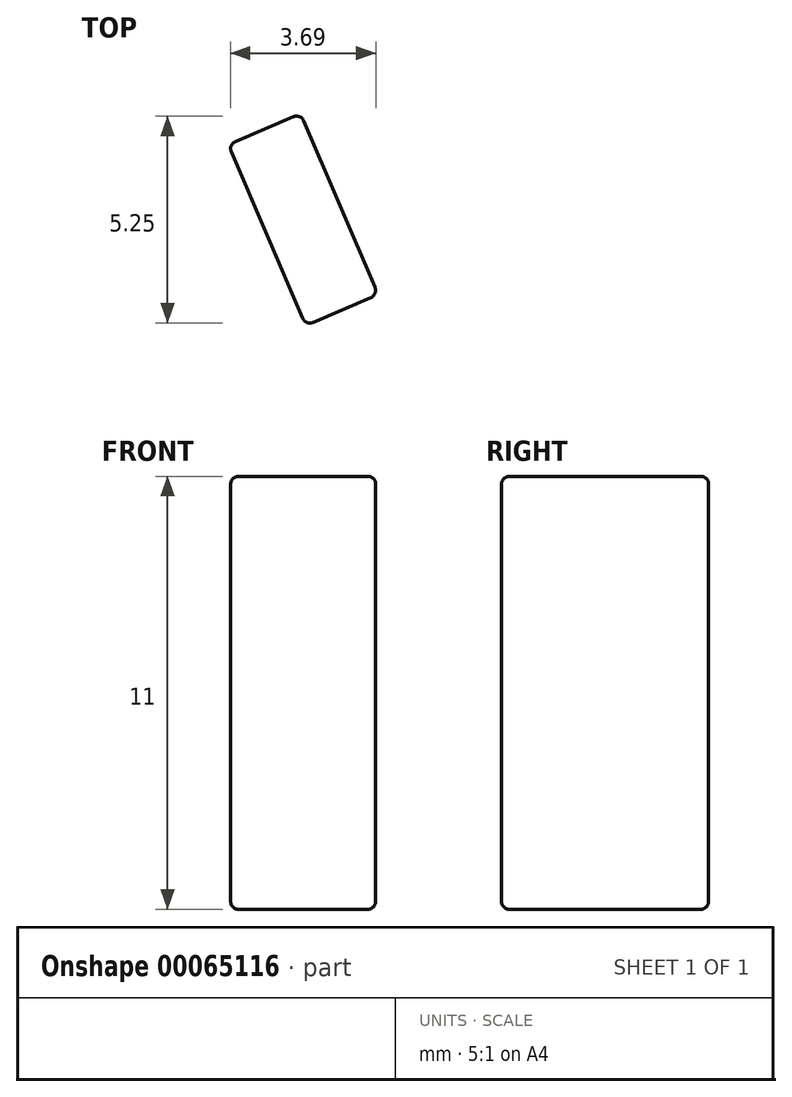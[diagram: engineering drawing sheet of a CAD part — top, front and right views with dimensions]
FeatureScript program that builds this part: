
annotation { "Feature Type Name" : "Feature", "Feature Type Description" : "" }
export const myFeature = defineFeature(function(context is Context, id is Id, definition is map)
    precondition{}
    {
        {
            var Q0;
            Q0=qCreatedBy(makeId("Top.planeOp"),FACE);
            var sketch = newSketch(context, id + "F0", { "sketchPlane" : qUnion([Q0])});
            skLineSegment(sketch, "E0", {"start": v(22.5, 2.5) * mm, "end": v(23.5, 15.5) * mm});
            skLineSegment(sketch, "E1", {"start": v(23.5, 15.5) * mm, "end": v(19, 26) * mm});
            skLineSegment(sketch, "E2", {"start": v(19, 26) * mm, "end": v(25.53, 26) * mm});
            skLineSegment(sketch, "E3", {"start": v(25.53, 26) * mm, "end": v(29.6, 16.5) * mm});
            skLineSegment(sketch, "E4", {"start": v(29.6, 16.5) * mm, "end": v(27.86, -6) * mm});
            skLineSegment(sketch, "E5", {"start": v(27.86, -6) * mm, "end": v(-27, -6) * mm});
            skLineSegment(sketch, "E6", {"start": v(-27, -6) * mm, "end": v(-36.5, 29.01) * mm});
            skLineSegment(sketch, "E7", {"start": v(-36.5, 29.01) * mm, "end": v(-36.5, 32) * mm});
            skLineSegment(sketch, "E8", {"start": v(-36.5, 32) * mm, "end": v(-18.5, 32) * mm});
            skLineSegment(sketch, "E9", {"start": v(-18.5, 32) * mm, "end": v(-18.5, 26) * mm});
            skLineSegment(sketch, "E10", {"start": v(-18.5, 26) * mm, "end": v(-23.5, 26) * mm});
            skLineSegment(sketch, "E11", {"start": v(-23.5, 26) * mm, "end": v(-26.7, 15.8) * mm});
            skLineSegment(sketch, "E12", {"start": v(-26.7, 15.8) * mm, "end": v(-23.5, 4) * mm});
            skLineSegment(sketch, "E13", {"start": v(-23.5, 4) * mm, "end": v(-19.5, 0) * mm});
            skLineSegment(sketch, "E14", {"start": v(-19.5, 0) * mm, "end": v(19.5, 0) * mm});
            skLineSegment(sketch, "E15", {"start": v(19.5, 0) * mm, "end": v(22.5, 2.5) * mm});
            skSolve(sketch);
        }
        {
            var Q0;
            Q0=qCreatedBy(makeId("Top.planeOp"),FACE);
            var sketch = newSketch(context, id + "F1", { "sketchPlane" : qUnion([Q0])});
            skLineSegment(sketch, "E16", {"start": v(22.8, 20.92) * mm, "end": v(24.65, 21.7) * mm});
            skLineSegment(sketch, "E17", {"start": v(24.65, 21.7) * mm, "end": v(26.62, 17.11) * mm});
            skLineSegment(sketch, "E18", {"start": v(26.62, 17.11) * mm, "end": v(24.78, 16.32) * mm});
            skLineSegment(sketch, "E19", {"start": v(24.78, 16.32) * mm, "end": v(22.8, 20.92) * mm});
            skLineSegment(sketch, "E20", {"start": v(-23.4, -1.5) * mm, "end": v(-18.4, -1.5) * mm, "construction": true});
            skLineSegment(sketch, "E21", {"start": v(-18.4, -1.5) * mm, "end": v(-18.4, -3.5) * mm, "construction": true});
            skLineSegment(sketch, "E22", {"start": v(-18.4, -3.5) * mm, "end": v(-23.4, -3.5) * mm, "construction": true});
            skLineSegment(sketch, "E23", {"start": v(-23.4, -3.5) * mm, "end": v(-23.4, -1.5) * mm, "construction": true});
            skLineSegment(sketch, "E24", {"start": v(-33.25, 26.58) * mm, "end": v(-31.32, 27.1) * mm, "construction": true});
            skLineSegment(sketch, "E25", {"start": v(-31.32, 27.1) * mm, "end": v(-30.01, 22.28) * mm, "construction": true});
            skLineSegment(sketch, "E26", {"start": v(-30.01, 22.28) * mm, "end": v(-31.94, 21.75) * mm, "construction": true});
            skLineSegment(sketch, "E27", {"start": v(-31.94, 21.75) * mm, "end": v(-33.25, 26.58) * mm, "construction": true});
            skLineSegment(sketch, "E28", {"start": v(-32.28, 26.84) * mm, "end": v(-30.98, 22.02) * mm, "construction": true});
            skLineSegment(sketch, "E29", {"start": v(-23.4, -2.5) * mm, "end": v(-18.4, -2.5) * mm, "construction": true});
            skLineSegment(sketch, "E30", {"start": v(25.7, 16.72) * mm, "end": v(23.73, 21.31) * mm, "construction": true});
            skLineSegment(sketch, "E31", {"start": v(-23.4, -3.5) * mm, "end": v(-27, -6) * mm, "construction": true});
            skLineSegment(sketch, "E32", {"start": v(-33.25, 26.58) * mm, "end": v(-36.5, 29.01) * mm, "construction": true});
            skLineSegment(sketch, "E33", {"start": v(24.65, 21.7) * mm, "end": v(25.53, 26) * mm, "construction": true});
            skSolve(sketch);
        }
        {
            var Q0;
            Q0=qSketchRegion(id+"F1",true);
            extrude(context, id + "F2", {"entities" : qUnion([Q0]), "depth" : 5.5 * mm});
        }
        {
            var Q0;
            Q0=makeQuery(id+"F2.opExtrude","SWEPT_BODY",BODY,{"disambiguationData":[OSD([sQuery(id+"F1.wireOp",EDGE,"E16"),sQuery(id+"F1.wireOp",EDGE,"E17"),sQuery(id+"F1.wireOp",EDGE,"E18"),sQuery(id+"F1.wireOp",EDGE,"E19")])]});
            var Q1;
            Q1=qCreatedBy(makeId("Top.planeOp"),FACE);
            mirror(context, id + "F3", {"operationType" : NewBodyOperationType.ADD, "entities" : qUnion([Q0]), "mirrorPlane" : qUnion([Q1])});
        }
        {
            var Q0;
            {var subQ0=makeQuery(id+"F2.opExtrude","SWEPT_FACE",FACE,{"disambiguationData":[OSD([sQuery(id+"F1.wireOp",EDGE,"E18")])]});Q0=makeQuery(id+"F3.boolean.opBoolean","MERGE",FACE,{"derivedFrom":[subQ0,makeQuery(id+"F3.opPattern","COPY",FACE,{"derivedFrom":subQ0,"instanceName":"1"})]});}
            var Q1;
            Q1=makeQuery(id+"F2.opExtrude","CAP_FACE",FACE,{"disambiguationData":[OSD([sQuery(id+"F1.wireOp",EDGE,"E16"),sQuery(id+"F1.wireOp",EDGE,"E17"),sQuery(id+"F1.wireOp",EDGE,"E18"),sQuery(id+"F1.wireOp",EDGE,"E19")])],"isStart":false});
            var Q2;
            {var subQ0=makeQuery(id+"F2.opExtrude","SWEPT_FACE",FACE,{"disambiguationData":[OSD([sQuery(id+"F1.wireOp",EDGE,"E16")])]});Q2=makeQuery(id+"F3.boolean.opBoolean","MERGE",FACE,{"derivedFrom":[subQ0,makeQuery(id+"F3.opPattern","COPY",FACE,{"derivedFrom":subQ0,"instanceName":"1"})]});}
            var Q3;
            Q3=makeQuery(id+"F3.opPattern","COPY",FACE,{"derivedFrom":makeQuery(id+"F2.opExtrude","CAP_FACE",FACE,{"disambiguationData":[OSD([sQuery(id+"F1.wireOp",EDGE,"E16"),sQuery(id+"F1.wireOp",EDGE,"E17"),sQuery(id+"F1.wireOp",EDGE,"E18"),sQuery(id+"F1.wireOp",EDGE,"E19")])],"isStart":false}),"instanceName":"1"});
            fillet(context, id + "F4", {"entities" : qUnion([Q0, Q1, Q2, Q3]), "radius" : .2 * mm, "tangentPropagation" : true, "allowEdgeOverflow" : false});
        }
    });
